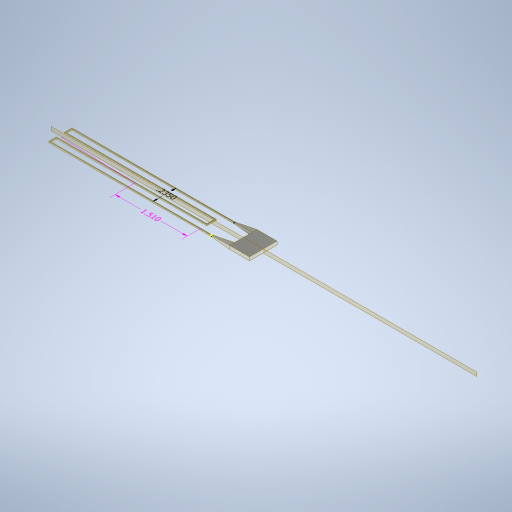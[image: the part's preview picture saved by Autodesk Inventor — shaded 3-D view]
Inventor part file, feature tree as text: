
AUTODESK INVENTOR PART (.ipt)
format: ipt  version: 2024.2 (Build 282272000, 272)  size: 342,016 bytes
history: native  units: in
note: dims shown in document units (in); Inventor stores cm internally (conversion verified against a paired STEP export)
features: sketch x7, other x4, plane x4, extrude x2, sweep x1, loft x1, mirror x1
ambient origin geometry x8: Origin, YZ Plane, XZ Plane, XY Plane, X Axis, Y Axis, Z Axis, Center Point
bodies: Solid1 (feature_tree)
feature tree (20):
  other  "Annotations"
  sweep  "Sweep1"
  plane  "Work Plane1"
  plane  "Work Plane2"
  sketch  "Sketch10"  dims[d24=0.01in d63=0.01in]
  extrude  "Extrusion7"  Depth=0.25in
  plane  "Work Plane3"
  sketch  "Sketch12"  dims[d67=0.08in]
  sketch  "Sketch13"  dims[d69=1.625in]
  loft  "Loft2"
  plane  "Work Plane4"
  mirror  "Mirror2"
  extrude  "Extrusion8"  Depth=0.08in
  sketch  "Sketch1"  dims[d4=0.05in d5=0.05in]
  sketch  "Sketch2"  dims[d6=0.0in d7=0.0in d11=0.25in d19=-0.25in]
  sketch  "Sketch11"  dims[d65=0.075in d66=0.08in]
  other  "Edges3"
  sketch  "Sketch14"  dims[d70=1.625in d71=1.0in d72=0.5in d73=0.0in d74=0.0in d75=0.2in d76=0.05in d77=0.0in d78=0.035in d79=0.0in d80=90.0deg d81=0.0in d82=90.0deg d86=-0.1175in d87=0.2in d88=0.0in d42=0.2341in d43=0.169in d44=0.235in d48=0.2141in d49=0.2512in d50=1.51in]
  other  "Linear Dimension 1"
  other  "Linear Dimension 3"
